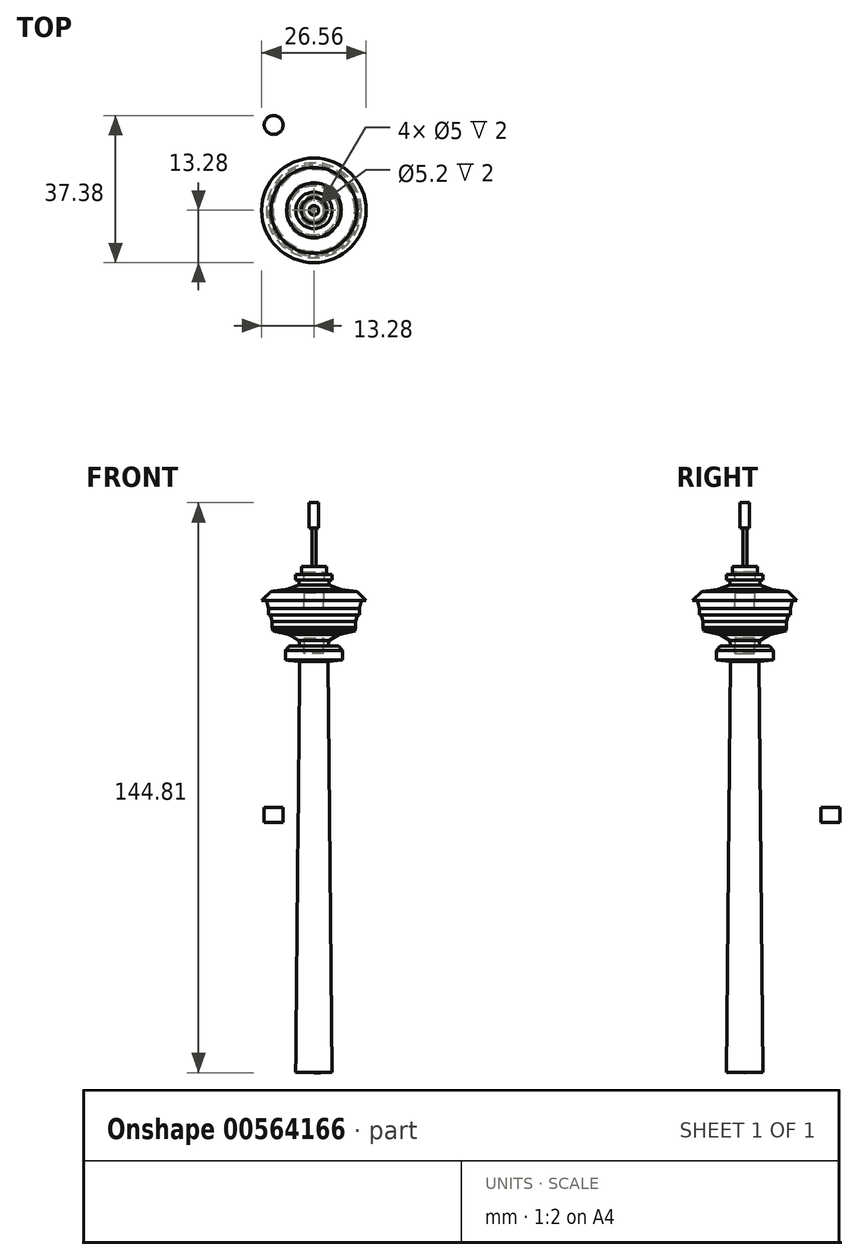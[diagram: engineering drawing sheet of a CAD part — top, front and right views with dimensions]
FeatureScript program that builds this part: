
annotation { "Feature Type Name" : "Feature", "Feature Type Description" : "" }
export const myFeature = defineFeature(function(context is Context, id is Id, definition is map)
    precondition{}
    {
        {
            var Q0;
            Q0=qCreatedBy(makeId("Front.planeOp"),FACE);
            var sketch = newSketch(context, id + "F0", { "sketchPlane" : qUnion([Q0])});
            skLineSegment(sketch, "E0", {"start": v(0, -67.7) * mm, "end": v(0, 74.4) * mm});
            skLineSegment(sketch, "E1", {"start": v(0, 74.4) * mm, "end": v(-1.22, 74.4) * mm});
            skLineSegment(sketch, "E2", {"start": v(-1.22, 74.4) * mm, "end": v(-1.22, 68) * mm});
            skLineSegment(sketch, "E3", {"start": v(-1.22, 68) * mm, "end": v(-0.53, 68) * mm});
            skLineSegment(sketch, "E4", {"start": v(-0.53, 68) * mm, "end": v(-0.53, 58.23) * mm});
            skLineSegment(sketch, "E5", {"start": v(-0.53, 58.23) * mm, "end": v(-3.21, 58.23) * mm});
            skLineSegment(sketch, "E6", {"start": v(-3.21, 58.23) * mm, "end": v(-3.21, 56.17) * mm});
            skLineSegment(sketch, "E7", {"start": v(-3.21, 56.17) * mm, "end": v(-4.63, 56.17) * mm});
            skLineSegment(sketch, "E8", {"start": v(-4.63, 56.17) * mm, "end": v(-4.63, 54.75) * mm});
            skLineSegment(sketch, "E9", {"start": v(-4.63, 54.75) * mm, "end": v(-3.78, 54.75) * mm});
            skLineSegment(sketch, "E10", {"start": v(-3.78, 54.75) * mm, "end": v(-3.78, 53.52) * mm});
            skLineSegment(sketch, "E11", {"start": v(-3.78, 53.52) * mm, "end": v(-6.93, 52.34) * mm});
            skLineSegment(sketch, "E12", {"start": v(-6.93, 52.34) * mm, "end": v(-10.9, 51.84) * mm});
            skLineSegment(sketch, "E13", {"start": v(-10.9, 51.84) * mm, "end": v(-13.28, 49.54) * mm});
            skLineSegment(sketch, "E14", {"start": v(-13.28, 49.54) * mm, "end": v(-12.06, 49.54) * mm});
            skLineSegment(sketch, "E15", {"start": v(-12.06, 49.54) * mm, "end": v(-11.56, 47.55) * mm});
            skLineSegment(sketch, "E16", {"start": v(-11.56, 47.55) * mm, "end": v(-11.56, 45.86) * mm});
            skLineSegment(sketch, "E17", {"start": v(-11.56, 45.86) * mm, "end": v(-11.02, 45.86) * mm});
            skLineSegment(sketch, "E18", {"start": v(-11.02, 45.86) * mm, "end": v(-10.6, 44.17) * mm});
            skLineSegment(sketch, "E19", {"start": v(-10.6, 44.17) * mm, "end": v(-10.6, 42.68) * mm});
            skLineSegment(sketch, "E20", {"start": v(-10.6, 42.68) * mm, "end": v(-10.4, 41.85) * mm});
            skLineSegment(sketch, "E21", {"start": v(-10.4, 41.85) * mm, "end": v(-6.36, 40.92) * mm});
            skLineSegment(sketch, "E22", {"start": v(-6.36, 40.92) * mm, "end": v(-3.78, 39.35) * mm});
            skLineSegment(sketch, "E23", {"start": v(-3.78, 39.35) * mm, "end": v(-3.62, 38.05) * mm});
            skLineSegment(sketch, "E24", {"start": v(-3.62, 38.05) * mm, "end": v(-6.2, 38.05) * mm});
            skLineSegment(sketch, "E25", {"start": v(-6.2, 38.05) * mm, "end": v(-7.23, 36.87) * mm});
            skLineSegment(sketch, "E26", {"start": v(-7.23, 36.87) * mm, "end": v(-7.23, 34.44) * mm});
            skLineSegment(sketch, "E27", {"start": v(-7.23, 34.44) * mm, "end": v(-3.62, 34.12) * mm});
            skLineSegment(sketch, "E28", {"start": v(-3.62, 34.12) * mm, "end": v(-4.63, -70.37) * mm});
            skLineSegment(sketch, "E29", {"start": v(-4.63, -70.37) * mm, "end": v(0, -70.41) * mm});
            skLineSegment(sketch, "E30", {"start": v(0, -70.41) * mm, "end": v(0, -67.7) * mm});
            skSolve(sketch);
        }
        {
            var Q0;
            Q0 = qSketchRegion(id + "F0", true);
            var Q1;
            Q1=sQuery(id+"F0.wireOp",EDGE,"E0");
            revolve(context, id + "F1", {"entities" : qUnion([Q0]), "axis" : qUnion([Q1]), "revolveType" : RevolveType.FULL});
        }
        {
            var Q0;
            Q0=qCreatedBy(makeId("Front.planeOp"),FACE);
            var sketch = newSketch(context, id + "F2", { "sketchPlane" : qUnion([Q0])});
            skLineSegment(sketch, "E31", {"start": v(-13.43, 49.53) * mm, "end": v(13.6, 49.53) * mm});
            skLineSegment(sketch, "E32", {"start": v(13.6, 49.53) * mm, "end": v(13.6, 49.54) * mm});
            skLineSegment(sketch, "E33", {"start": v(13.6, 49.54) * mm, "end": v(-13.43, 49.54) * mm});
            skLineSegment(sketch, "E34", {"start": v(-13.43, 49.54) * mm, "end": v(-13.43, 49.53) * mm});
            skLineSegment(sketch, "E35", {"start": v(-6.2, 38.05) * mm, "end": v(7.26, 38.05) * mm});
            skLineSegment(sketch, "E36", {"start": v(7.26, 38.05) * mm, "end": v(7.26, 38.06) * mm});
            skLineSegment(sketch, "E37", {"start": v(7.26, 38.06) * mm, "end": v(-6.2, 38.06) * mm});
            skLineSegment(sketch, "E38", {"start": v(-6.2, 38.06) * mm, "end": v(-6.2, 38.05) * mm});
            skLineSegment(sketch, "E39", {"start": v(-4.5, 54.75) * mm, "end": v(5.64, 54.75) * mm});
            skLineSegment(sketch, "E40", {"start": v(5.64, 54.75) * mm, "end": v(5.64, 54.74) * mm});
            skLineSegment(sketch, "E41", {"start": v(5.64, 54.74) * mm, "end": v(-4.5, 54.74) * mm});
            skLineSegment(sketch, "E42", {"start": v(-4.5, 54.74) * mm, "end": v(-4.5, 54.75) * mm});
            skSolve(sketch);
        }
        {
            var Q0;
            Q0 = qSketchRegion(id + "F2", true);
            extrude(context, id + "F3", {"entities" : qUnion([Q0]), "operationType" : NewBodyOperationType.REMOVE, "depth" : 25 * mm, "offsetDistance" : 25 * mm, "hasSecondDirection" : true, "secondDirectionOppositeDirection" : true, "secondDirectionDepth" : 25 * mm});
        }
        {
            var Q0;
            Q0=makeQuery(id+"F3.boolean.opBoolean","SPLIT",BODY,{"disambiguationData":[OD(0.0)],"derivedFrom":makeQuery(id+"F1.opRevolve","SWEPT_BODY",BODY,{"disambiguationData":[OSD([sQuery(id+"F0.wireOp",EDGE,"E0"),sQuery(id+"F0.wireOp",EDGE,"E1"),sQuery(id+"F0.wireOp",EDGE,"E2"),sQuery(id+"F0.wireOp",EDGE,"E3"),sQuery(id+"F0.wireOp",EDGE,"E4"),sQuery(id+"F0.wireOp",EDGE,"E5"),sQuery(id+"F0.wireOp",EDGE,"E6"),sQuery(id+"F0.wireOp",EDGE,"E7"),sQuery(id+"F0.wireOp",EDGE,"E8"),sQuery(id+"F0.wireOp",EDGE,"E9"),sQuery(id+"F0.wireOp",EDGE,"E10"),sQuery(id+"F0.wireOp",EDGE,"E11"),sQuery(id+"F0.wireOp",EDGE,"E12"),sQuery(id+"F0.wireOp",EDGE,"E13"),sQuery(id+"F0.wireOp",EDGE,"E14"),sQuery(id+"F0.wireOp",EDGE,"E15"),sQuery(id+"F0.wireOp",EDGE,"E16"),sQuery(id+"F0.wireOp",EDGE,"E17"),sQuery(id+"F0.wireOp",EDGE,"E18"),sQuery(id+"F0.wireOp",EDGE,"E19"),sQuery(id+"F0.wireOp",EDGE,"E20"),sQuery(id+"F0.wireOp",EDGE,"E21"),sQuery(id+"F0.wireOp",EDGE,"E22"),sQuery(id+"F0.wireOp",EDGE,"E23"),sQuery(id+"F0.wireOp",EDGE,"E24"),sQuery(id+"F0.wireOp",EDGE,"E25"),sQuery(id+"F0.wireOp",EDGE,"E26"),sQuery(id+"F0.wireOp",EDGE,"E27"),sQuery(id+"F0.wireOp",EDGE,"E28"),sQuery(id+"F0.wireOp",EDGE,"E29"),sQuery(id+"F0.wireOp",EDGE,"E30")])]})});
            transform(context, id + "F4", {"entities" : qUnion([Q0]), "transformType" : TransformType.TRANSLATION_3D, "dx" : 0 * mm, "dy" : 0 * mm, "dz" : 12.4 * mm, "makeCopy" : false});
        }
        {
            var Q0;
            Q0=makeQuery(id+"F3.boolean.opBoolean","SPLIT",BODY,{"disambiguationData":[OD(1.0)],"derivedFrom":makeQuery(id+"F1.opRevolve","SWEPT_BODY",BODY,{"disambiguationData":[OSD([sQuery(id+"F0.wireOp",EDGE,"E0"),sQuery(id+"F0.wireOp",EDGE,"E1"),sQuery(id+"F0.wireOp",EDGE,"E2"),sQuery(id+"F0.wireOp",EDGE,"E3"),sQuery(id+"F0.wireOp",EDGE,"E4"),sQuery(id+"F0.wireOp",EDGE,"E5"),sQuery(id+"F0.wireOp",EDGE,"E6"),sQuery(id+"F0.wireOp",EDGE,"E7"),sQuery(id+"F0.wireOp",EDGE,"E8"),sQuery(id+"F0.wireOp",EDGE,"E9"),sQuery(id+"F0.wireOp",EDGE,"E10"),sQuery(id+"F0.wireOp",EDGE,"E11"),sQuery(id+"F0.wireOp",EDGE,"E12"),sQuery(id+"F0.wireOp",EDGE,"E13"),sQuery(id+"F0.wireOp",EDGE,"E14"),sQuery(id+"F0.wireOp",EDGE,"E15"),sQuery(id+"F0.wireOp",EDGE,"E16"),sQuery(id+"F0.wireOp",EDGE,"E17"),sQuery(id+"F0.wireOp",EDGE,"E18"),sQuery(id+"F0.wireOp",EDGE,"E19"),sQuery(id+"F0.wireOp",EDGE,"E20"),sQuery(id+"F0.wireOp",EDGE,"E21"),sQuery(id+"F0.wireOp",EDGE,"E22"),sQuery(id+"F0.wireOp",EDGE,"E23"),sQuery(id+"F0.wireOp",EDGE,"E24"),sQuery(id+"F0.wireOp",EDGE,"E25"),sQuery(id+"F0.wireOp",EDGE,"E26"),sQuery(id+"F0.wireOp",EDGE,"E27"),sQuery(id+"F0.wireOp",EDGE,"E28"),sQuery(id+"F0.wireOp",EDGE,"E29"),sQuery(id+"F0.wireOp",EDGE,"E30")])]})});
            transform(context, id + "F5", {"entities" : qUnion([Q0]), "transformType" : TransformType.TRANSLATION_3D, "dx" : 0 * mm, "dy" : 0 * mm, "dz" : 7.1 * mm, "makeCopy" : false});
        }
        {
            var Q0;
            Q0=makeQuery(id+"F3.boolean.opBoolean","SPLIT",BODY,{"disambiguationData":[OD(3.0)],"derivedFrom":makeQuery(id+"F1.opRevolve","SWEPT_BODY",BODY,{"disambiguationData":[OSD([sQuery(id+"F0.wireOp",EDGE,"E0"),sQuery(id+"F0.wireOp",EDGE,"E1"),sQuery(id+"F0.wireOp",EDGE,"E2"),sQuery(id+"F0.wireOp",EDGE,"E3"),sQuery(id+"F0.wireOp",EDGE,"E4"),sQuery(id+"F0.wireOp",EDGE,"E5"),sQuery(id+"F0.wireOp",EDGE,"E6"),sQuery(id+"F0.wireOp",EDGE,"E7"),sQuery(id+"F0.wireOp",EDGE,"E8"),sQuery(id+"F0.wireOp",EDGE,"E9"),sQuery(id+"F0.wireOp",EDGE,"E10"),sQuery(id+"F0.wireOp",EDGE,"E11"),sQuery(id+"F0.wireOp",EDGE,"E12"),sQuery(id+"F0.wireOp",EDGE,"E13"),sQuery(id+"F0.wireOp",EDGE,"E14"),sQuery(id+"F0.wireOp",EDGE,"E15"),sQuery(id+"F0.wireOp",EDGE,"E16"),sQuery(id+"F0.wireOp",EDGE,"E17"),sQuery(id+"F0.wireOp",EDGE,"E18"),sQuery(id+"F0.wireOp",EDGE,"E19"),sQuery(id+"F0.wireOp",EDGE,"E20"),sQuery(id+"F0.wireOp",EDGE,"E21"),sQuery(id+"F0.wireOp",EDGE,"E22"),sQuery(id+"F0.wireOp",EDGE,"E23"),sQuery(id+"F0.wireOp",EDGE,"E24"),sQuery(id+"F0.wireOp",EDGE,"E25"),sQuery(id+"F0.wireOp",EDGE,"E26"),sQuery(id+"F0.wireOp",EDGE,"E27"),sQuery(id+"F0.wireOp",EDGE,"E28"),sQuery(id+"F0.wireOp",EDGE,"E29"),sQuery(id+"F0.wireOp",EDGE,"E30")])]})});
            transform(context, id + "F6", {"entities" : qUnion([Q0]), "transformType" : TransformType.TRANSLATION_3D, "dx" : 0 * mm, "dy" : 0 * mm, "dz" : -12.7 * mm, "makeCopy" : false});
        }
        {
            var Q0;
            Q0=makeQuery(id+"F3.boolean.opBoolean","MERGE",FACE,{"derivedFrom":[makeQuery(id+"F1.opRevolve","SWEPT_FACE",FACE,{"disambiguationData":[OSD([sQuery(id+"F0.wireOp",EDGE,"E24")])]}),makeQuery(id+"F3.opExtrude","SWEPT_FACE",FACE,{"disambiguationData":[OSD([sQuery(id+"F2.wireOp",EDGE,"E35")])]})]});
            var sketch = newSketch(context, id + "F7", { "sketchPlane" : qUnion([Q0])});
            skCircle(sketch, "E43", {"center": v(0, 0) * mm, "radius": 2.5 * mm});
            skSolve(sketch);
        }
        {
            var Q0;
            Q0 = qSketchRegion(id + "F7", true);
            extrude(context, id + "F8", {"entities" : qUnion([Q0]), "operationType" : NewBodyOperationType.REMOVE, "oppositeDirection" : true, "depth" : 2 * mm, "offsetDistance" : 25 * mm});
        }
        {
            var Q0;
            Q0=makeQuery(id+"F3.boolean.opBoolean","COPY",FACE,{"derivedFrom":makeQuery(id+"F3.opExtrude","SWEPT_FACE",FACE,{"disambiguationData":[OSD([sQuery(id+"F2.wireOp",EDGE,"E37")])]})});
            var sketch = newSketch(context, id + "F9", { "sketchPlane" : qUnion([Q0])});
            skCircle(sketch, "E44", {"center": v(0, 0) * mm, "radius": 2.5 * mm});
            skSolve(sketch);
        }
        {
            var Q0;
            Q0 = qSketchRegion(id + "F9", true);
            extrude(context, id + "F10", {"entities" : qUnion([Q0]), "operationType" : NewBodyOperationType.REMOVE, "oppositeDirection" : true, "depth" : 2 * mm, "offsetDistance" : 25 * mm});
        }
        {
            var Q0;
            Q0=makeQuery(id+"F3.boolean.opBoolean","COPY",FACE,{"derivedFrom":makeQuery(id+"F3.opExtrude","SWEPT_FACE",FACE,{"disambiguationData":[OSD([sQuery(id+"F2.wireOp",EDGE,"E31")])]})});
            var sketch = newSketch(context, id + "F11", { "sketchPlane" : qUnion([Q0])});
            skCircle(sketch, "E45", {"center": v(0, 0) * mm, "radius": 2.5 * mm});
            skSolve(sketch);
        }
        {
            var Q0;
            Q0 = qSketchRegion(id + "F11", true);
            extrude(context, id + "F12", {"entities" : qUnion([Q0]), "operationType" : NewBodyOperationType.REMOVE, "oppositeDirection" : true, "depth" : 2 * mm, "offsetDistance" : 25 * mm});
        }
        {
            var Q0;
            Q0=makeQuery(id+"F3.boolean.opBoolean","MERGE",FACE,{"derivedFrom":[makeQuery(id+"F1.opRevolve","SWEPT_FACE",FACE,{"disambiguationData":[OSD([sQuery(id+"F0.wireOp",EDGE,"E14")])]}),makeQuery(id+"F3.opExtrude","SWEPT_FACE",FACE,{"disambiguationData":[OSD([sQuery(id+"F2.wireOp",EDGE,"E33")])]})]});
            var sketch = newSketch(context, id + "F13", { "sketchPlane" : qUnion([Q0])});
            skCircle(sketch, "E46", {"center": v(0, 0) * mm, "radius": 2.5 * mm});
            skSolve(sketch);
        }
        {
            var Q0;
            Q0 = qSketchRegion(id + "F13", true);
            extrude(context, id + "F14", {"entities" : qUnion([Q0]), "operationType" : NewBodyOperationType.REMOVE, "oppositeDirection" : true, "depth" : 2 * mm, "offsetDistance" : 25 * mm});
        }
        {
            var Q0;
            Q0=makeQuery(id+"F3.boolean.opBoolean","COPY",FACE,{"derivedFrom":makeQuery(id+"F3.opExtrude","SWEPT_FACE",FACE,{"disambiguationData":[OSD([sQuery(id+"F2.wireOp",EDGE,"E41")])]})});
            var sketch = newSketch(context, id + "F15", { "sketchPlane" : qUnion([Q0])});
            skCircle(sketch, "E47", {"center": v(0, 0) * mm, "radius": 2.5 * mm});
            skSolve(sketch);
        }
        {
            var Q0;
            Q0 = qSketchRegion(id + "F15", true);
            extrude(context, id + "F16", {"entities" : qUnion([Q0]), "operationType" : NewBodyOperationType.ADD, "depth" : 2 * mm, "offsetDistance" : 25 * mm});
        }
        {
            var Q0;
            Q0=makeQuery(id+"F3.boolean.opBoolean","MERGE",FACE,{"derivedFrom":[makeQuery(id+"F1.opRevolve","SWEPT_FACE",FACE,{"disambiguationData":[OSD([sQuery(id+"F0.wireOp",EDGE,"E9")])]}),makeQuery(id+"F3.opExtrude","SWEPT_FACE",FACE,{"disambiguationData":[OSD([sQuery(id+"F2.wireOp",EDGE,"E39")])]})]});
            var sketch = newSketch(context, id + "F17", { "sketchPlane" : qUnion([Q0])});
            skCircle(sketch, "E48", {"center": v(0, 0) * mm, "radius": 2.6 * mm});
            skSolve(sketch);
        }
        {
            var Q0;
            Q0 = qSketchRegion(id + "F17", true);
            extrude(context, id + "F18", {"entities" : qUnion([Q0]), "operationType" : NewBodyOperationType.REMOVE, "oppositeDirection" : true, "depth" : 2 * mm, "offsetDistance" : 25 * mm});
        }
        {
            var Q0;
            Q0=qCreatedBy(makeId("Top.planeOp"),FACE);
            var sketch = newSketch(context, id + "F19", { "sketchPlane" : qUnion([Q0])});
            skCircle(sketch, "E49", {"center": v(-10.22, 21.7) * mm, "radius": 2.4 * mm});
            skSolve(sketch);
        }
        {
            var Q0;
            Q0 = qSketchRegion(id + "F19", true);
            extrude(context, id + "F20", {"entities" : qUnion([Q0]), "depth" : 3.8 * mm, "offsetDistance" : 25 * mm});
        }
    });
